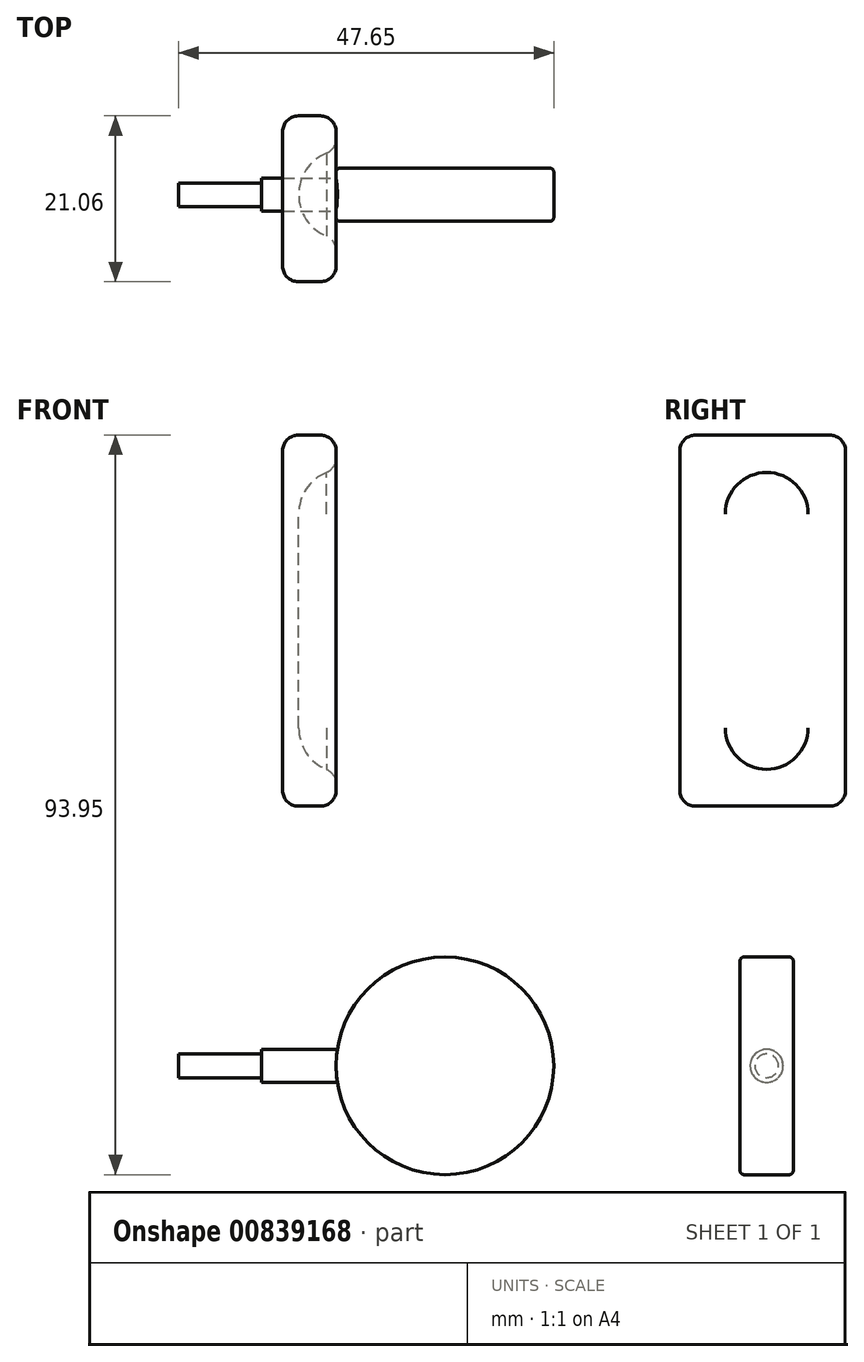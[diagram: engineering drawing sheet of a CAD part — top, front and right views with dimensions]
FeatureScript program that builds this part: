
annotation { "Feature Type Name" : "Feature", "Feature Type Description" : "" }
export const myFeature = defineFeature(function(context is Context, id is Id, definition is map)
    precondition{}
    {
        {
            var Q0;
            Q0=qCreatedBy(makeId("Front.planeOp"),FACE);
            var sketch = newSketch(context, id + "F0", { "sketchPlane" : qUnion([Q0])});
            skLineSegment(sketch, "E0.bottom", {"start": v(-4.75, 5.93) * mm, "end": v(28.45, 5.93) * mm});
            skLineSegment(sketch, "E0.top", {"start": v(-4.75, -32.65) * mm, "end": v(28.45, -32.65) * mm});
            skLineSegment(sketch, "E0.left", {"start": v(-4.75, 5.93) * mm, "end": v(-4.75, -32.65) * mm});
            skLineSegment(sketch, "E0.right", {"start": v(28.45, 5.93) * mm, "end": v(28.45, -32.65) * mm});
            skLineSegment(sketch, "E1", {"start": v(0, 9.16) * mm, "end": v(0, -34.52) * mm, "construction": true});
            skPoint(sketch, "E2", {"position": v(0, 5.93) * mm});
            skSolve(sketch);
        }
        {
            var Q0;
            Q0=makeQuery(id+"F0.imprint","IMPRINT",FACE,{"disambiguationData":[TD([[makeQuery(id+"F0.imprint","IMPRINT",EDGE,{"derivedFrom":sQuery(id+"F0.wireOp",EDGE,"E0.bottom")}),-1.0]])]});
            extrude(context, id + "F1", {"entities" : qUnion([Q0]), "endBound" : BoundingType.SYMMETRIC, "depth" : 11.4 * mm, "offsetDistance" : 25 * mm});
        }
        {
            var Q0;
            Q0=makeQuery(id+"F1.opExtrude","CAP_FACE",FACE,{"disambiguationData":[OSD([sQuery(id+"F0.wireOp",EDGE,"E0.bottom"),sQuery(id+"F0.wireOp",EDGE,"E0.top"),sQuery(id+"F0.wireOp",EDGE,"E0.left"),sQuery(id+"F0.wireOp",EDGE,"E0.right")])],"isStart":false});
            var Q1;
            Q1=makeQuery(id+"F1.opExtrude","CAP_FACE",FACE,{"disambiguationData":[OSD([sQuery(id+"F0.wireOp",EDGE,"E0.bottom"),sQuery(id+"F0.wireOp",EDGE,"E0.top"),sQuery(id+"F0.wireOp",EDGE,"E0.left"),sQuery(id+"F0.wireOp",EDGE,"E0.right")])],"isStart":true});
            fillet(context, id + "F2", {"entities" : qUnion([Q0, Q1]), "tangentPropagation" : true, "radius" : 5.7 * mm, "defaultsChanged" : false, "vertexSettings" : [], "allowEdgeOverflow" : false});
        }
        {
            var Q0;
            Q0=makeQuery(id+"F2.opFillet","BLEND_EDGE",EDGE,{"blendedFrom":[makeQuery(id+"F1.opExtrude","CAP_EDGE",EDGE,{"disambiguationData":[OSD([sQuery(id+"F0.wireOp",EDGE,"E0.top")])],"isStart":true}),makeQuery(id+"F1.opExtrude","CAP_EDGE",EDGE,{"disambiguationData":[OSD([sQuery(id+"F0.wireOp",EDGE,"E0.right")])],"isStart":true})],"blendedInto":[]});
            var Q1;
            Q1=makeQuery(id+"F2.opFillet","BLEND_EDGE",EDGE,{"blendedFrom":[makeQuery(id+"F1.opExtrude","CAP_EDGE",EDGE,{"disambiguationData":[OSD([sQuery(id+"F0.wireOp",EDGE,"E0.top")])],"isStart":true}),makeQuery(id+"F1.opExtrude","CAP_EDGE",EDGE,{"disambiguationData":[OSD([sQuery(id+"F0.wireOp",EDGE,"E0.left")])],"isStart":true})],"blendedInto":[]});
            var Q2;
            Q2=makeQuery(id+"F2.opFillet","BLEND_EDGE",EDGE,{"blendedFrom":[makeQuery(id+"F1.opExtrude","CAP_EDGE",EDGE,{"disambiguationData":[OSD([sQuery(id+"F0.wireOp",EDGE,"E0.bottom")])],"isStart":true}),makeQuery(id+"F1.opExtrude","CAP_EDGE",EDGE,{"disambiguationData":[OSD([sQuery(id+"F0.wireOp",EDGE,"E0.left")])],"isStart":true})],"blendedInto":[]});
            var Q3;
            Q3=makeQuery(id+"F2.opFillet","BLEND_EDGE",EDGE,{"blendedFrom":[makeQuery(id+"F1.opExtrude","CAP_EDGE",EDGE,{"disambiguationData":[OSD([sQuery(id+"F0.wireOp",EDGE,"E0.bottom")])],"isStart":true}),makeQuery(id+"F1.opExtrude","CAP_EDGE",EDGE,{"disambiguationData":[OSD([sQuery(id+"F0.wireOp",EDGE,"E0.right")])],"isStart":true})],"blendedInto":[]});
            fillet(context, id + "F3", {"entities" : qUnion([Q0, Q1, Q2, Q3]), "tangentPropagation" : true, "radius" : 5.7 * mm, "defaultsChanged" : false, "vertexSettings" : [], "allowEdgeOverflow" : false});
        }
        {
            var Q0;
            Q0=qCreatedBy(makeId("Right.planeOp"),FACE);
            var sketch = newSketch(context, id + "F4", { "sketchPlane" : qUnion([Q0])});
            skLineSegment(sketch, "E3.bottom", {"start": v(10.02, 10.24) * mm, "end": v(-11.04, 10.24) * mm});
            skLineSegment(sketch, "E3.top", {"start": v(10.02, -36.9) * mm, "end": v(-11.04, -36.9) * mm});
            skLineSegment(sketch, "E3.left", {"start": v(10.02, 10.24) * mm, "end": v(10.02, -36.9) * mm});
            skLineSegment(sketch, "E3.right", {"start": v(-11.04, 10.24) * mm, "end": v(-11.04, -36.9) * mm});
            skSolve(sketch);
        }
        {
            var Q0;
            Q0=makeQuery(id+"F4.imprint","IMPRINT",FACE,{"disambiguationData":[TD([[makeQuery(id+"F4.imprint","IMPRINT",EDGE,{"derivedFrom":sQuery(id+"F4.wireOp",EDGE,"E3.bottom")}),1.0]])]});
            extrude(context, id + "F5", {"entities" : qUnion([Q0]), "oppositeDirection" : true, "depth" : 6.8 * mm, "offsetDistance" : 25 * mm});
        }
        {
            var Q0;
            Q0=makeQuery(id+"F1.opExtrude","SWEPT_BODY",BODY,{"disambiguationData":[OSD([sQuery(id+"F0.wireOp",EDGE,"E0.bottom"),sQuery(id+"F0.wireOp",EDGE,"E0.top"),sQuery(id+"F0.wireOp",EDGE,"E0.left"),sQuery(id+"F0.wireOp",EDGE,"E0.right")])]});
            var Q1;
            Q1=makeQuery(id+"F5.opExtrude","SWEPT_BODY",BODY,{"disambiguationData":[OSD([sQuery(id+"F4.wireOp",EDGE,"E3.bottom"),sQuery(id+"F4.wireOp",EDGE,"E3.top"),sQuery(id+"F4.wireOp",EDGE,"E3.left"),sQuery(id+"F4.wireOp",EDGE,"E3.right")])]});
            booleanBodies(context, id + "F6", {"operationType" : BooleanOperationType.SUBTRACTION, "tools" : qUnion([Q0]), "targets" : qUnion([Q1])});
        }
        {
            var Q0;
            Q0=makeQuery(id+"F5.opExtrude","SWEPT_FACE",FACE,{"disambiguationData":[OSD([sQuery(id+"F4.wireOp",EDGE,"E3.right")])]});
            var Q1;
            Q1=makeQuery(id+"F5.opExtrude","CAP_FACE",FACE,{"disambiguationData":[OSD([sQuery(id+"F4.wireOp",EDGE,"E3.bottom"),sQuery(id+"F4.wireOp",EDGE,"E3.top"),sQuery(id+"F4.wireOp",EDGE,"E3.left"),sQuery(id+"F4.wireOp",EDGE,"E3.right")])],"isStart":true});
            var Q2;
            Q2=makeQuery(id+"F5.opExtrude","CAP_FACE",FACE,{"disambiguationData":[OSD([sQuery(id+"F4.wireOp",EDGE,"E3.bottom"),sQuery(id+"F4.wireOp",EDGE,"E3.top"),sQuery(id+"F4.wireOp",EDGE,"E3.left"),sQuery(id+"F4.wireOp",EDGE,"E3.right")])],"isStart":false});
            var Q3;
            Q3=makeQuery(id+"F5.opExtrude","SWEPT_FACE",FACE,{"disambiguationData":[OSD([sQuery(id+"F4.wireOp",EDGE,"E3.left")])]});
            fillet(context, id + "F7", {"entities" : qUnion([Q0, Q1, Q2, Q3]), "tangentPropagation" : true, "radius" : 2 * mm, "defaultsChanged" : false, "vertexSettings" : [], "allowEdgeOverflow" : false});
        }
        {
            var Q0;
            Q0=qCreatedBy(makeId("Right.planeOp"),FACE);
            var sketch = newSketch(context, id + "F8", { "sketchPlane" : qUnion([Q0])});
            skLineSegment(sketch, "E4", {"start": v(2.88, -83.7) * mm, "end": v(-2.88, -83.7) * mm, "construction": true});
            skLineSegment(sketch, "E5", {"start": v(-2.88, -56.06) * mm, "end": v(2.88, -56.06) * mm, "construction": true});
            skLineSegment(sketch, "E6.0", {"start": v(3.38, -56.56) * mm, "end": v(3.38, -83.2) * mm, "construction": true});
            skLineSegment(sketch, "E7.0", {"start": v(-3.38, -83.2) * mm, "end": v(-3.38, -56.56) * mm, "construction": true});
            skLineSegment(sketch, "E8", {"start": v(0, -87.56) * mm, "end": v(0, -49.17) * mm, "construction": true});
            skPoint(sketch, "E8.startSnap0", {"position": v(0, -83.7) * mm});
            skPoint(sketch, "E8.endSnap0", {"position": v(0, -56.06) * mm});
            skLineSegment(sketch, "E9", {"start": v(-7.1, -69.88) * mm, "end": v(6.22, -69.88) * mm, "construction": true});
            skPoint(sketch, "E9.startSnap0", {"position": v(-3.38, -69.88) * mm});
            skCircle(sketch, "E10", {"center": v(0, -69.88) * mm, "radius": 2.1 * mm});
            skCircle(sketch, "E11", {"center": v(0, -69.88) * mm, "radius": 1.5 * mm});
            skSolve(sketch);
        }
        {
            var Q0;
            Q0=qCreatedBy(makeId("Front.planeOp"),FACE);
            var sketch = newSketch(context, id + "F9", { "sketchPlane" : qUnion([Q0])});
            skCircle(sketch, "E12", {"center": v(13.82, -69.88) * mm, "radius": 13.82 * mm});
            skLineSegment(sketch, "E13", {"start": v(33.94, -69.88) * mm, "end": v(-7.58, -69.88) * mm, "construction": true});
            skLineSegment(sketch, "E14", {"start": v(13.83, -50.2) * mm, "end": v(13.83, -96.14) * mm, "construction": true});
            skPoint(sketch, "E15", {"position": v(0, -69.88) * mm});
            skSolve(sketch);
        }
        {
            var Q0;
            Q0=makeQuery(id+"F9.imprint","IMPRINT",FACE,{"disambiguationData":[TD([[makeQuery(id+"F9.imprint","IMPRINT",EDGE,{"derivedFrom":sQuery(id+"F9.wireOp",EDGE,"E12")}),1.0]])]});
            extrude(context, id + "F10", {"entities" : qUnion([Q0]), "endBound" : BoundingType.SYMMETRIC, "depth" : 6.75 * mm, "offsetDistance" : 25 * mm});
        }
        {
            var Q0;
            Q0=makeQuery(id+"F8.imprint","IMPRINT",FACE,{"disambiguationData":[TD([[makeQuery(id+"F8.imprint","IMPRINT",EDGE,{"derivedFrom":sQuery(id+"F8.wireOp",EDGE,"E10")}),1.0]])]});
            var Q1;
            Q1=makeQuery(id+"F8.imprint","IMPRINT",FACE,{"disambiguationData":[TD([[makeQuery(id+"F8.imprint","IMPRINT",EDGE,{"derivedFrom":sQuery(id+"F8.wireOp",EDGE,"E11")}),1.0]])]});
            extrude(context, id + "F11", {"entities" : qUnion([Q0, Q1]), "oppositeDirection" : true, "depth" : 9.5 * mm, "offsetDistance" : 25 * mm});
        }
        {
            var Q0;
            Q0=makeQuery(id+"F10.opExtrude","CAP_FACE",FACE,{"disambiguationData":[OSD([sQuery(id+"F9.wireOp",EDGE,"E12")])],"isStart":false});
            var Q1;
            Q1=makeQuery(id+"F10.opExtrude","CAP_FACE",FACE,{"disambiguationData":[OSD([sQuery(id+"F9.wireOp",EDGE,"E12")])],"isStart":true});
            fillet(context, id + "F12", {"entities" : qUnion([Q0, Q1]), "tangentPropagation" : true, "radius" : .5 * mm, "defaultsChanged" : true, "vertexSettings" : [], "allowEdgeOverflow" : false});
        }
        {
            var Q0;
            Q0=makeQuery(id+"F8.imprint","IMPRINT",FACE,{"disambiguationData":[TD([[makeQuery(id+"F8.imprint","IMPRINT",EDGE,{"derivedFrom":sQuery(id+"F8.wireOp",EDGE,"E11")}),1.0]])]});
            extrude(context, id + "F13", {"entities" : qUnion([Q0]), "operationType" : NewBodyOperationType.ADD, "oppositeDirection" : true, "depth" : 20 * mm, "offsetDistance" : 25 * mm});
        }
        {
            var Q0;
            Q0=makeQuery(id+"F8.imprint","IMPRINT",FACE,{"disambiguationData":[TD([[makeQuery(id+"F8.imprint","IMPRINT",EDGE,{"derivedFrom":sQuery(id+"F8.wireOp",EDGE,"E10")}),1.0]])]});
            var Q1;
            Q1=makeQuery(id+"F8.imprint","IMPRINT",FACE,{"disambiguationData":[TD([[makeQuery(id+"F8.imprint","IMPRINT",EDGE,{"derivedFrom":sQuery(id+"F8.wireOp",EDGE,"E11")}),1.0]])]});
            extrude(context, id + "F14", {"entities" : qUnion([Q0, Q1]), "operationType" : NewBodyOperationType.ADD, "depth" : 1.65 * mm, "offsetDistance" : 25 * mm});
        }
    });
